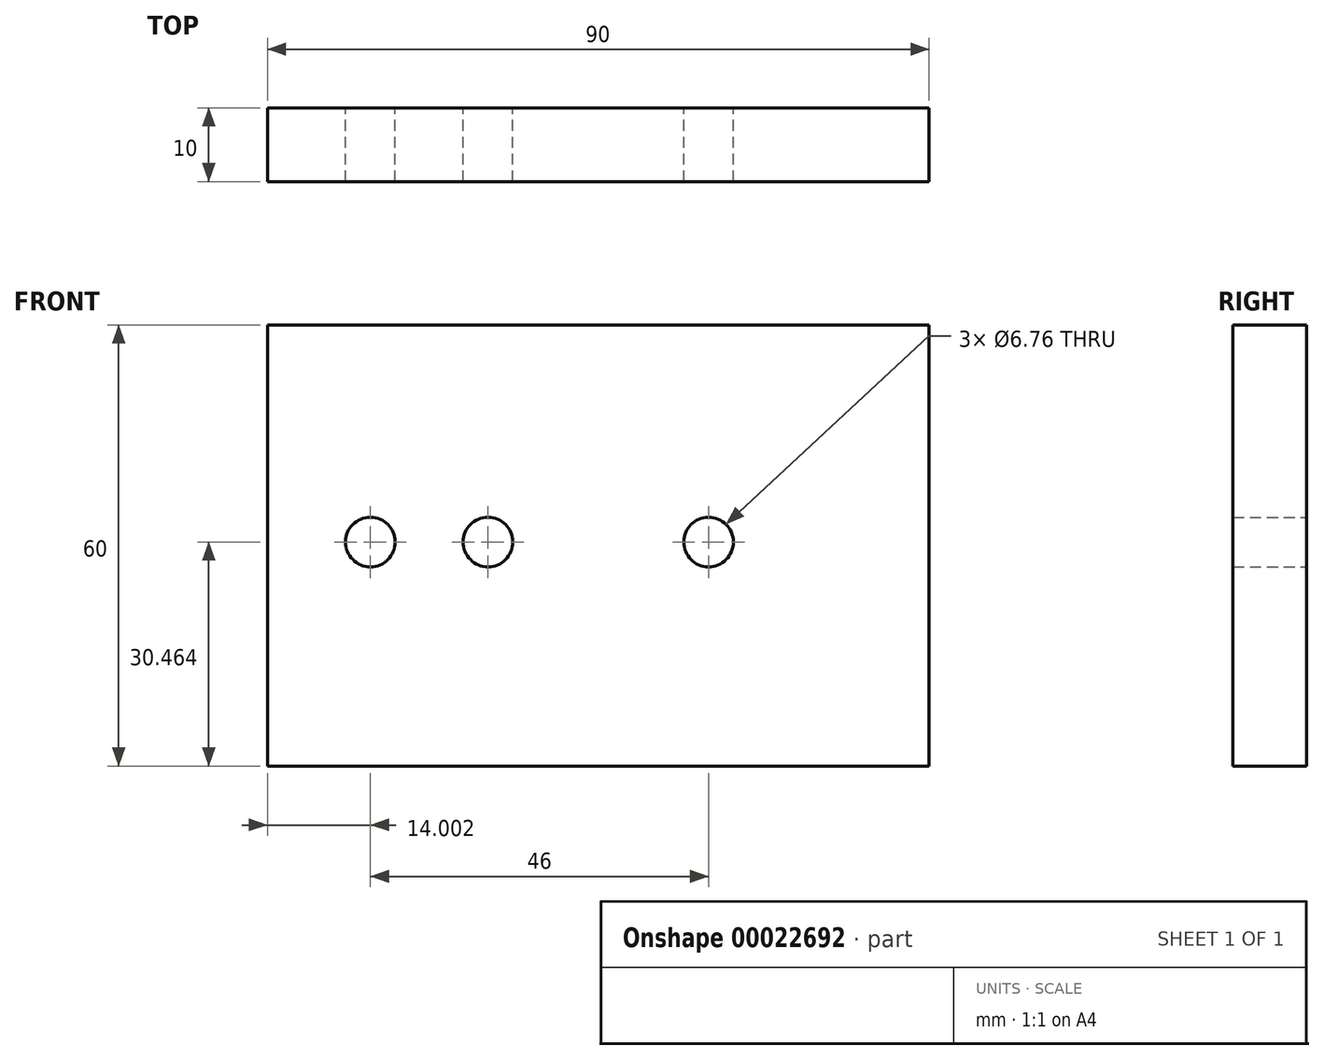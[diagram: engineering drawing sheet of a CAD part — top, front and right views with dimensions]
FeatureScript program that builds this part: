
annotation { "Feature Type Name" : "Feature", "Feature Type Description" : "" }
export const myFeature = defineFeature(function(context is Context, id is Id, definition is map)
    precondition{}
    {
        {
            var Q0;
            Q0=qCreatedBy(makeId("Front.planeOp"),FACE);
            var sketch = newSketch(context, id + "F0", { "sketchPlane" : qUnion([Q0])});
            skLineSegment(sketch, "E0", {"start": v(-44, 33.49) * mm, "end": v(46, 33.49) * mm});
            skLineSegment(sketch, "E1", {"start": v(46, 33.49) * mm, "end": v(46, -26.51) * mm});
            skLineSegment(sketch, "E2", {"start": v(46, -26.51) * mm, "end": v(-44, -26.51) * mm});
            skCircle(sketch, "E3", {"center": v(-14, 3.95) * mm, "radius": 3.38 * mm});
            skCircle(sketch, "E4", {"center": v(16, 3.95) * mm, "radius": 3.38 * mm});
            skCircle(sketch, "E5", {"center": v(-30, 3.95) * mm, "radius": 3.38 * mm});
            skLineSegment(sketch, "E6", {"start": v(-44, 33.49) * mm, "end": v(-44, -26.51) * mm});
            skSolve(sketch);
        }
        {
            var Q0;
            Q0=makeQuery(id+"F0.imprint","IMPRINT",FACE,{"disambiguationData":[TD([[makeQuery(id+"F0.imprint","IMPRINT",EDGE,{"derivedFrom":sQuery(id+"F0.wireOp",EDGE,"E0")}),-1.0]])]});
            extrude(context, id + "F1", {"entities" : qUnion([Q0]), "depth" : 10 * mm});
        }
    });
